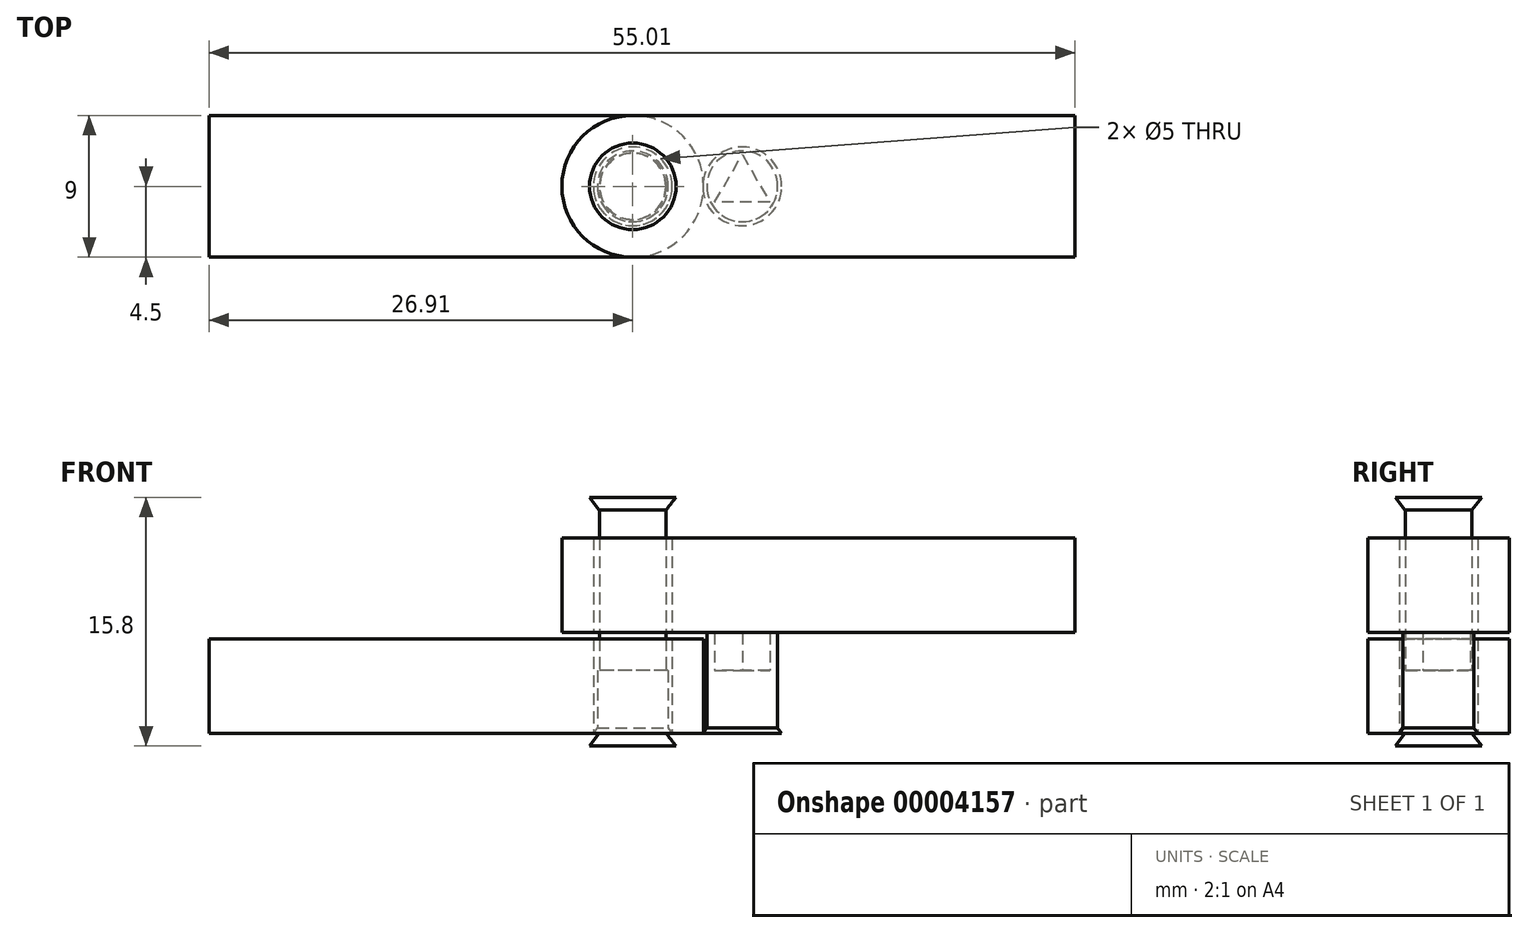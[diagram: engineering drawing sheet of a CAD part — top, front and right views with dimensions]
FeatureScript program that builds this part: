
annotation { "Feature Type Name" : "Feature", "Feature Type Description" : "" }
export const myFeature = defineFeature(function(context is Context, id is Id, definition is map)
    precondition{}
    {
        {
            var Q0;
            Q0=qCreatedBy(makeId("Top.planeOp"),FACE);
            var sketch = newSketch(context, id + "F0", { "sketchPlane" : qUnion([Q0])});
            skCircle(sketch, "E0", {"center": v(0, 0) * mm, "radius": 2.5 * mm});
            skCircle(sketch, "E1", {"center": v(0, 0) * mm, "radius": 4.5 * mm});
            skLineSegment(sketch, "E2", {"start": v(0, 4.5) * mm, "end": v(28.1, 4.5) * mm});
            skLineSegment(sketch, "E3", {"start": v(0, -4.5) * mm, "end": v(28.1, -4.5) * mm});
            skLineSegment(sketch, "E4", {"start": v(0, -4.5) * mm, "end": v(-26.9, -4.5) * mm});
            skLineSegment(sketch, "E5", {"start": v(0, 4.5) * mm, "end": v(-26.9, 4.5) * mm});
            skLineSegment(sketch, "E6", {"start": v(-26.9, 4.5) * mm, "end": v(-26.9, -4.5) * mm});
            skLineSegment(sketch, "E7", {"start": v(28.1, 4.5) * mm, "end": v(28.1, -4.5) * mm});
            skSolve(sketch);
        }
        {
            var Q0;
            Q0=qCreatedBy(makeId("Top.planeOp"),FACE);
            cPlane(context, id + "F1", {"entities" : qUnion([Q0]), "cplaneType" : CPlaneType.OFFSET, "offset" : .8 * mm, "oppositeDirection" : true, "width" : 150 * mm, "height" : 150 * mm});
        }
        {
            var Q0;
            Q0=qCreatedBy(id+"F1.planeOp",FACE);
            var sketch = newSketch(context, id + "F2", { "sketchPlane" : qUnion([Q0])});
            skCircle(sketch, "E8", {"center": v(0, 0) * mm, "radius": 2.75 * mm});
            skCircle(sketch, "E9", {"center": v(0, 0) * mm, "radius": 2.1 * mm});
            skSolve(sketch);
        }
        {
            var Q0;
            Q0=makeQuery(id+"F2.imprint","IMPRINT",FACE,{"disambiguationData":[TD([[makeQuery(id+"F2.imprint","IMPRINT",EDGE,{"derivedFrom":sQuery(id+"F2.wireOp",EDGE,"E8")}),1.0]])]});
            var Q1;
            Q1=makeQuery(id+"F2.imprint","IMPRINT",FACE,{"disambiguationData":[TD([[makeQuery(id+"F2.imprint","IMPRINT",EDGE,{"derivedFrom":sQuery(id+"F2.wireOp",EDGE,"E9")}),1.0]])]});
            extrude(context, id + "F3", {"entities" : qUnion([Q0, Q1]), "depth" : .8 * mm});
        }
        {
            var Q0;
            Q0=makeQuery(id+"F2.imprint","IMPRINT",FACE,{"disambiguationData":[TD([[makeQuery(id+"F2.imprint","IMPRINT",EDGE,{"derivedFrom":sQuery(id+"F2.wireOp",EDGE,"E9")}),1.0]])]});
            extrude(context, id + "F4", {"entities" : qUnion([Q0]), "operationType" : NewBodyOperationType.ADD, "depth" : 15 * mm});
        }
        {
            var Q0;
            Q0=makeQuery(id+"F4.opExtrude","CAP_FACE",FACE,{"disambiguationData":[OSD([sQuery(id+"F2.wireOp",EDGE,"E9")])],"isStart":false});
            var sketch = newSketch(context, id + "F5", { "sketchPlane" : qUnion([Q0])});
            skCircle(sketch, "E10.0", {"center": v(0, 0) * mm, "radius": 2.75 * mm});
            skSolve(sketch);
        }
        {
            var Q0;
            {var subQ0=makeQuery(id+"F5.imprint","IMPRINT",EDGE,{"derivedFrom":makeQuery(id+"F4.opExtrude","CAP_EDGE",EDGE,{"disambiguationData":[OSD([sQuery(id+"F2.wireOp",EDGE,"E9")])],"isStart":false})});Q0=qUnion([makeQuery(id+"F5.imprint","IMPRINT",FACE,{"disambiguationData":[TD([[makeQuery(id+"F5.imprint","IMPRINT",EDGE,{"derivedFrom":sQuery(id+"F5.wireOp",EDGE,"E10.0")}),1.0]])]}),makeQuery(id+"F5.imprint","IMPRINT",FACE,{"disambiguationData":[TD([[subQ0,1.0]])]})]);}
            extrude(context, id + "F6", {"entities" : qUnion([Q0]), "operationType" : NewBodyOperationType.ADD, "depth" : .8 * mm});
        }
        {
            var Q0;
            Q0=makeQuery(id+"F3.opExtrude","CAP_EDGE",EDGE,{"disambiguationData":[OSD([sQuery(id+"F2.wireOp",EDGE,"E8")])],"isStart":false});
            chamfer(context, id + "F7", {"entities" : qUnion([Q0]), "chamferType" : ChamferType.OFFSET_ANGLE, "width" : .8 * mm, "oppositeDirection" : true, "angle" : 38 * degree, "tangentPropagation" : true});
        }
        {
            var Q0;
            Q0=makeQuery(id+"F6.opExtrude","CAP_EDGE",EDGE,{"disambiguationData":[OSD([sQuery(id+"F5.wireOp",EDGE,"E10.0")])],"isStart":true});
            chamfer(context, id + "F8", {"entities" : qUnion([Q0]), "chamferType" : ChamferType.OFFSET_ANGLE, "width" : .8 * mm, "oppositeDirection" : false, "angle" : 38 * degree, "tangentPropagation" : true});
        }
        {
            var Q0;
            {var subQ1=sQuery(id+"F0.wireOp",EDGE,"E4");Q0=makeQuery(id+"F0.imprint","IMPRINT",FACE,{"disambiguationData":[TD([[makeQuery(id+"F0.imprint","IMPRINT",EDGE,{"derivedFrom":subQ1}),-1.0]])]});}
            var Q1;
            Q1=makeQuery(id+"F0.imprint","IMPRINT",FACE,{"disambiguationData":[TD([[makeQuery(id+"F0.imprint","IMPRINT",EDGE,{"derivedFrom":sQuery(id+"F0.wireOp",EDGE,"E0")}),-1.0]])]});
            extrude(context, id + "F9", {"entities" : qUnion([Q0, Q1]), "depth" : 6 * mm});
        }
        {
            var Q0;
            Q0=makeQuery(id+"F9.opExtrude","CAP_FACE",FACE,{"disambiguationData":[OSD([sQuery(id+"F0.wireOp",EDGE,"E0"),sQuery(id+"F0.wireOp",EDGE,"E1"),sQuery(id+"F0.wireOp",EDGE,"E4"),sQuery(id+"F0.wireOp",EDGE,"E5"),sQuery(id+"F0.wireOp",EDGE,"E6")])],"isStart":false});
            cPlane(context, id + "F10", {"entities" : qUnion([Q0]), "cplaneType" : CPlaneType.OFFSET, "offset" : .4 * mm, "width" : 150 * mm, "height" : 150 * mm});
        }
        {
            var Q0;
            Q0=qCreatedBy(id+"F10.planeOp",FACE);
            var sketch = newSketch(context, id + "F11", { "sketchPlane" : qUnion([Q0])});
            skLineSegment(sketch, "E11.0.0", {"start": v(0, 4.5) * mm, "end": v(28.1, 4.5) * mm});
            skArc(sketch, "E11.0.1", {"start": v(0, -4.5) * mm, "mid": v(4.5, 0) * mm, "end": v(0, 4.5) * mm});
            skLineSegment(sketch, "E11.0.2", {"start": v(0, -4.5) * mm, "end": v(28.1, -4.5) * mm});
            skLineSegment(sketch, "E11.0.3", {"start": v(28.1, 4.5) * mm, "end": v(28.1, -4.5) * mm});
            skCircle(sketch, "E12.0", {"center": v(0, 0) * mm, "radius": 4.5 * mm});
            skCircle(sketch, "E13.0", {"center": v(0, 0) * mm, "radius": 2.5 * mm});
            skSolve(sketch);
        }
        {
            var Q0;
            {var subQ3=sQuery(id+"F11.wireOp",EDGE,"E11.0.0");Q0=qUnion([makeQuery(id+"F11.imprint","IMPRINT",FACE,{"disambiguationData":[TD([[makeQuery(id+"F11.imprint","IMPRINT",EDGE,{"derivedFrom":subQ3}),-1.0]])]}),makeQuery(id+"F11.imprint","IMPRINT",FACE,{"disambiguationData":[TD([[makeQuery(id+"F11.imprint","IMPRINT",EDGE,{"derivedFrom":sQuery(id+"F11.wireOp",EDGE,"E13.0")}),-1.0]])]})]);}
            extrude(context, id + "F12", {"entities" : qUnion([Q0]), "depth" : 6 * mm});
        }
        {
            var Q0;
            Q0=qCreatedBy(makeId("Top.planeOp"),FACE);
            var sketch = newSketch(context, id + "F13", { "sketchPlane" : qUnion([Q0])});
            skCircle(sketch, "E14", {"center": v(0, 0) * mm, "radius": 2.5 * mm});
            skSolve(sketch);
        }
        {
            var Q0;
            Q0=makeQuery(id+"F13.imprint","IMPRINT",FACE,{"disambiguationData":[TD([[makeQuery(id+"F13.imprint","IMPRINT",EDGE,{"derivedFrom":sQuery(id+"F13.wireOp",EDGE,"E14")}),1.0]])]});
            extrude(context, id + "F14", {"entities" : qUnion([Q0]), "depth" : .8 * mm});
        }
        {
            var Q0;
            Q0=makeQuery(id+"F14.opExtrude","CAP_FACE",FACE,{"disambiguationData":[OSD([sQuery(id+"F13.wireOp",EDGE,"E14")])],"isStart":false});
            var sketch = newSketch(context, id + "F15", { "sketchPlane" : qUnion([Q0])});
            skCircle(sketch, "E15", {"center": v(0, 0) * mm, "radius": 2.25 * mm});
            skSolve(sketch);
        }
        {
            var Q0;
            Q0=makeQuery(id+"F15.imprint","IMPRINT",FACE,{"disambiguationData":[TD([[makeQuery(id+"F15.imprint","IMPRINT",EDGE,{"derivedFrom":sQuery(id+"F15.wireOp",EDGE,"E15")}),1.0]])]});
            extrude(context, id + "F16", {"entities" : qUnion([Q0]), "operationType" : NewBodyOperationType.ADD, "depth" : (4 - .8) * mm});
        }
        {
            var Q0;
            Q0=makeQuery(id+"F16.opExtrude","CAP_FACE",FACE,{"disambiguationData":[OSD([sQuery(id+"F15.wireOp",EDGE,"E15")])],"isStart":false});
            var sketch = newSketch(context, id + "F17", { "sketchPlane" : qUnion([Q0])});
            skPoint(sketch, "E16.0", {"position": v(0, 0) * mm});
            skLineSegment(sketch, "E17", {"start": v(1.5, -0.87) * mm, "end": v(-1.5, -0.87) * mm});
            skLineSegment(sketch, "E18", {"start": v(-1.5, -0.87) * mm, "end": v(0, 1.73) * mm});
            skLineSegment(sketch, "E19", {"start": v(0, 1.73) * mm, "end": v(1.5, -0.87) * mm});
            skLineSegment(sketch, "E20", {"start": v(0.75, 0.43) * mm, "end": v(-1.5, -0.87) * mm, "construction": true});
            skLineSegment(sketch, "E21", {"start": v(0, 1.73) * mm, "end": v(0, -0.87) * mm, "construction": true});
            skSolve(sketch);
        }
        {
            var Q0;
            Q0=makeQuery(id+"F17.imprint","IMPRINT",FACE,{"disambiguationData":[TD([[makeQuery(id+"F17.imprint","IMPRINT",EDGE,{"derivedFrom":sQuery(id+"F17.wireOp",EDGE,"E17")}),-1.0]])]});
            extrude(context, id + "F18", {"entities" : qUnion([Q0]), "operationType" : NewBodyOperationType.ADD, "depth" : 4 * mm});
        }
        {
            var Q0;
            Q0=makeQuery(id+"F14.opExtrude","CAP_EDGE",EDGE,{"disambiguationData":[OSD([sQuery(id+"F13.wireOp",EDGE,"E14")])],"isStart":false});
            chamfer(context, id + "F19", {"entities" : qUnion([Q0]), "chamferType" : ChamferType.OFFSET_ANGLE, "width" : .8 * mm, "oppositeDirection" : true, "angle" : 35 * degree, "tangentPropagation" : true});
        }
        {
            var Q0;
            Q0=qCreatedBy(makeId("Top.planeOp"),FACE);
            var sketch = newSketch(context, id + "F20", { "sketchPlane" : qUnion([Q0])});
            skCircle(sketch, "E22", {"center": v(6.96, 0) * mm, "radius": 2.5 * mm});
            skSolve(sketch);
        }
        {
            var Q0;
            Q0=makeQuery(id+"F20.imprint","IMPRINT",FACE,{"disambiguationData":[TD([[makeQuery(id+"F20.imprint","IMPRINT",EDGE,{"derivedFrom":sQuery(id+"F20.wireOp",EDGE,"E22")}),1.0]])]});
            extrude(context, id + "F21", {"entities" : qUnion([Q0]), "depth" : .8 * mm});
        }
        {
            var Q0;
            Q0=makeQuery(id+"F21.opExtrude","CAP_FACE",FACE,{"disambiguationData":[OSD([sQuery(id+"F20.wireOp",EDGE,"E22")])],"isStart":false});
            var sketch = newSketch(context, id + "F22", { "sketchPlane" : qUnion([Q0])});
            skCircle(sketch, "E23.0", {"center": v(6.96, 0) * mm, "radius": 2.5 * mm});
            skCircle(sketch, "E24", {"center": v(6.96, 0) * mm, "radius": 2.25 * mm});
            skSolve(sketch);
        }
        {
            var Q0;
            Q0=makeQuery(id+"F22.imprint","IMPRINT",FACE,{"disambiguationData":[TD([[makeQuery(id+"F22.imprint","IMPRINT",EDGE,{"derivedFrom":sQuery(id+"F22.wireOp",EDGE,"E24")}),1.0]])]});
            extrude(context, id + "F23", {"entities" : qUnion([Q0]), "operationType" : NewBodyOperationType.ADD, "depth" : (4 - .8) * mm});
        }
        {
            var Q0;
            Q0=makeQuery(id+"F21.opExtrude","CAP_EDGE",EDGE,{"disambiguationData":[OSD([sQuery(id+"F20.wireOp",EDGE,"E22")])],"isStart":false});
            chamfer(context, id + "F24", {"entities" : qUnion([Q0]), "chamferType" : ChamferType.OFFSET_ANGLE, "width" : .8 * mm, "oppositeDirection" : true, "angle" : 35 * degree, "tangentPropagation" : true});
        }
        {
            var Q0;
            Q0=makeQuery(id+"F23.opExtrude","CAP_FACE",FACE,{"disambiguationData":[OSD([sQuery(id+"F22.wireOp",EDGE,"E24")])],"isStart":false});
            var sketch = newSketch(context, id + "F25", { "sketchPlane" : qUnion([Q0])});
            skLineSegment(sketch, "E25", {"start": v(8.7, -1.01) * mm, "end": v(5.2, -1.01) * mm});
            skLineSegment(sketch, "E26", {"start": v(5.2, -1.01) * mm, "end": v(6.96, 2.02) * mm});
            skLineSegment(sketch, "E27", {"start": v(6.96, 2.02) * mm, "end": v(8.7, -1.01) * mm});
            skLineSegment(sketch, "E28", {"start": v(7.83, 0.5) * mm, "end": v(5.2, -1.01) * mm, "construction": true});
            skLineSegment(sketch, "E29", {"start": v(6.08, 0.5) * mm, "end": v(8.7, -1.01) * mm, "construction": true});
            skPoint(sketch, "E30", {"position": v(6.96, 0) * mm});
            skCircle(sketch, "E31.0", {"center": v(6.96, 0) * mm, "radius": 2.25 * mm});
            skSolve(sketch);
        }
        {
            var Q0;
            Q0=makeQuery(id+"F25.imprint","IMPRINT",FACE,{"disambiguationData":[TD([[makeQuery(id+"F25.imprint","IMPRINT",EDGE,{"derivedFrom":sQuery(id+"F25.wireOp",EDGE,"E25")}),1.0]])]});
            extrude(context, id + "F26", {"entities" : qUnion([Q0]), "operationType" : NewBodyOperationType.ADD, "depth" : 4 * mm});
        }
    });
